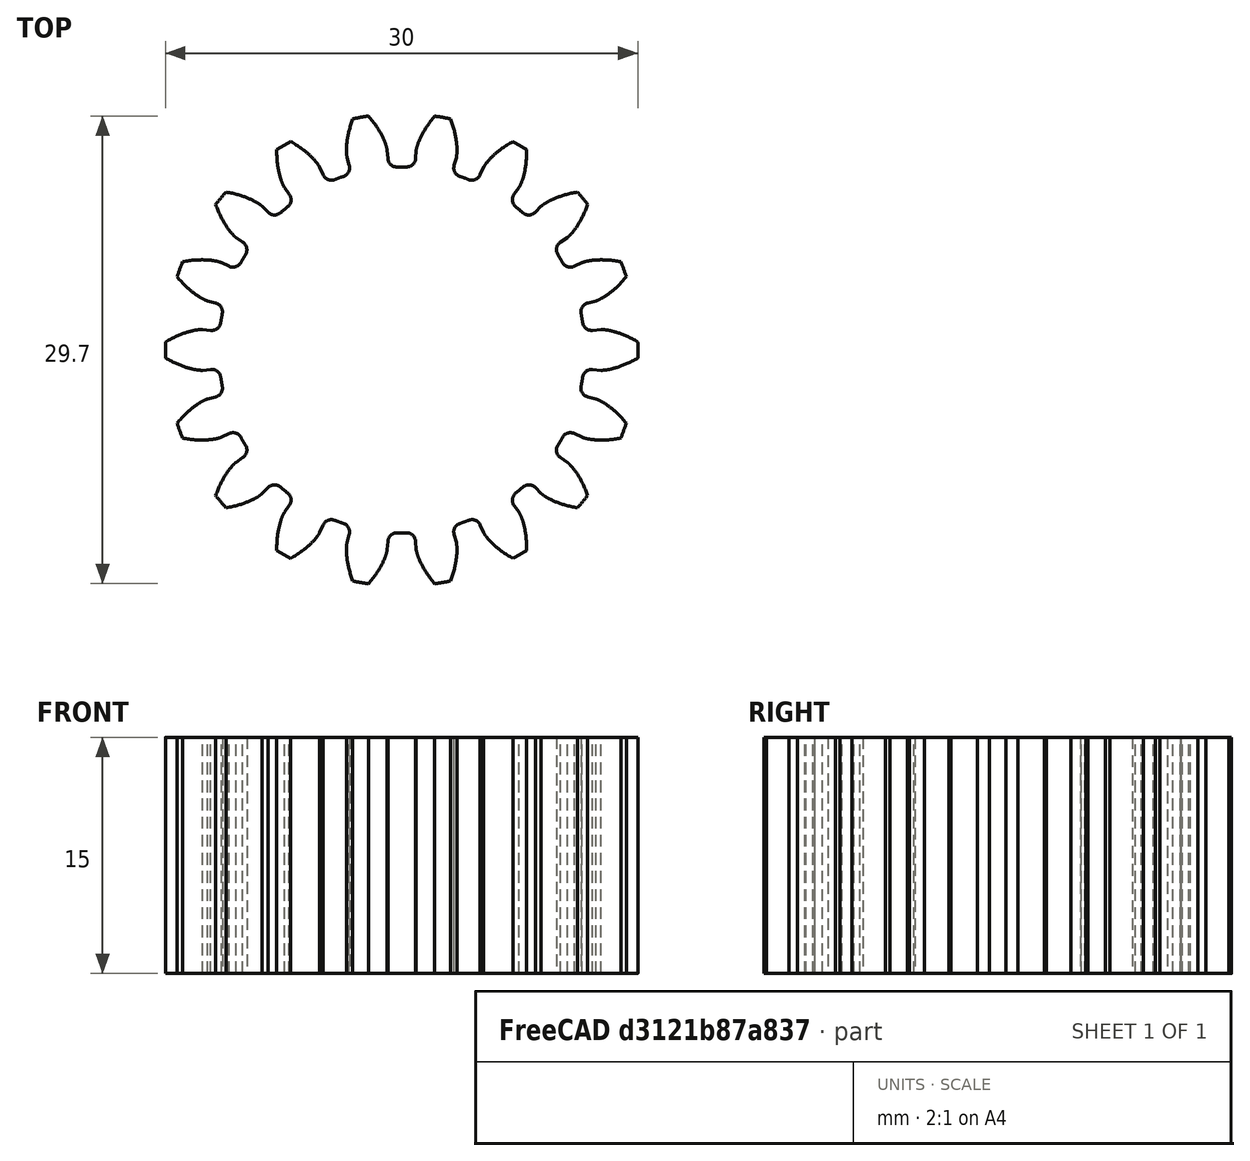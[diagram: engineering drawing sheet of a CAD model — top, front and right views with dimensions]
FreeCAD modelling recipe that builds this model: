
FCSTD DOCUMENT  (FreeCAD 1.0R39319 (Git))
Label: inv gear t18 m1_5 w15
License: All rights reserved
LicenseURL: https://en.wikipedia.org/wiki/All_rights_reserved
objects: Part::Part2DObjectPython×1, PartDesign::Pad×1, PartDesign::Body×1
note: 5 computed .brp shape members not serialized (recipe doc carries the construction recipe); baked Part::Feature solids carry a one-line shape summary decoded from their .brp

FEATURE [Part::Part2DObjectPython] InvoluteGear  # Draft 2D object (typed FeaturePython)
  AddendumCoefficient = 1
  DedendumCoefficient = 1.25
  ExternalGear = true
  HighPrecision = true
  Modules = 1.5
  NumberOfTeeth = 18
  PressureAngle = 20
  ProfileShiftCoefficient = 0
  RootFilletCoefficient = 0.38
FEATURE [PartDesign::Pad] Pad
  Direction = (0,0,1)
  Length = 15
  Length2 = 10
  Profile = -> InvoluteGear
  ReferenceAxis = -> InvoluteGear [N_Axis]
  Refine = true
  Suppressed = false
  Type = 0
FEATURE [PartDesign::Body] Body
  AllowCompound = false
  Group = -> [InvoluteGear,Pad]
  Origin = -> Origin
  Tip = -> Pad
